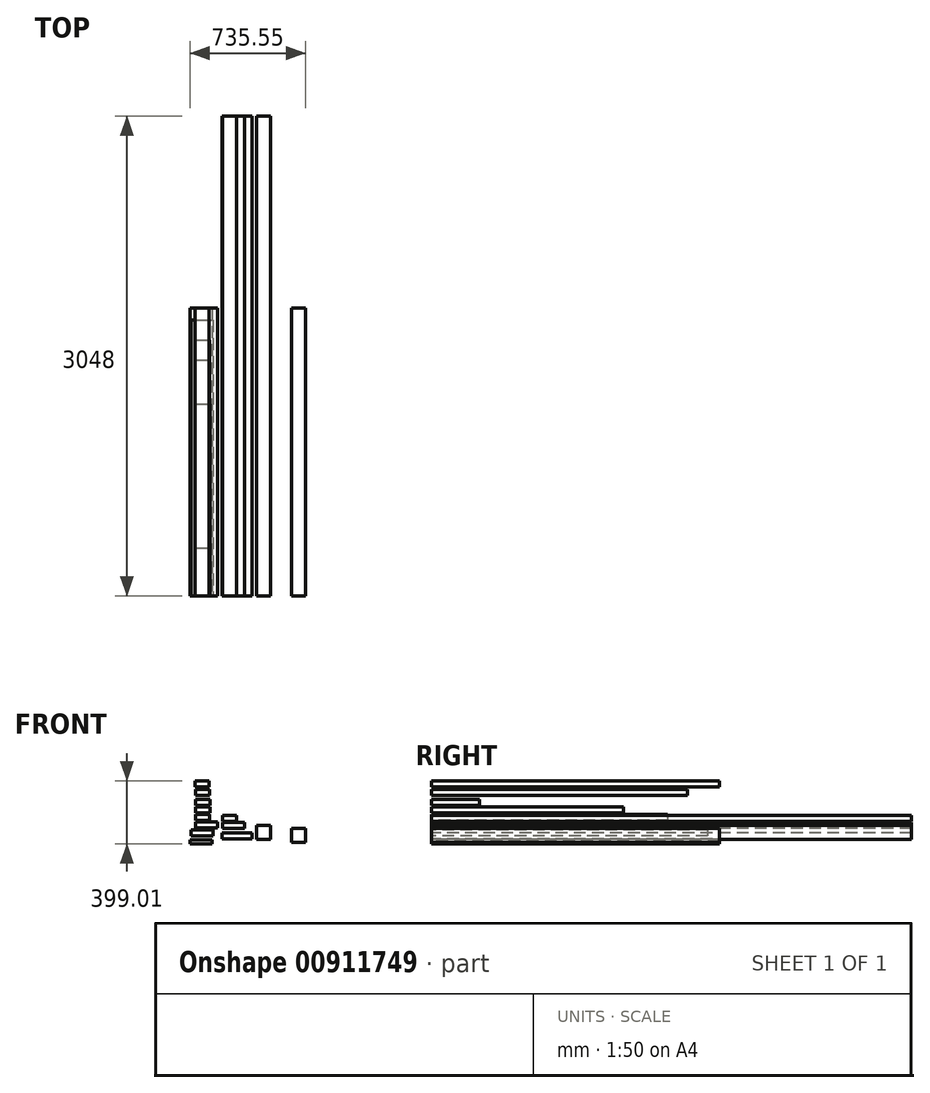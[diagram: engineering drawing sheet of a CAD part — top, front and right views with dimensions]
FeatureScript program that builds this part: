
annotation { "Feature Type Name" : "Feature", "Feature Type Description" : "" }
export const myFeature = defineFeature(function(context is Context, id is Id, definition is map)
    precondition{}
    {
        {
            var Q0;
            Q0=qCreatedBy(makeId("Front.planeOp"),FACE);
            var sketch = newSketch(context, id + "F0", { "sketchPlane" : qUnion([Q0])});
            skLineSegment(sketch, "E0.bottom", {"start": v(-255.68, 9.52) * mm, "end": v(-115.94, 9.52) * mm});
            skLineSegment(sketch, "E0.top", {"start": v(-255.68, -28.56) * mm, "end": v(-115.94, -28.56) * mm});
            skLineSegment(sketch, "E0.left", {"start": v(-255.68, 9.52) * mm, "end": v(-255.68, -28.56) * mm});
            skLineSegment(sketch, "E0.right", {"start": v(-115.94, 9.52) * mm, "end": v(-115.94, -28.56) * mm});
            skLineSegment(sketch, "E1.bottom", {"start": v(-256.83, 16.75) * mm, "end": v(-167.73, 16.75) * mm});
            skLineSegment(sketch, "E1.top", {"start": v(-256.83, 54.83) * mm, "end": v(-167.73, 54.83) * mm});
            skLineSegment(sketch, "E1.left", {"start": v(-256.83, 16.75) * mm, "end": v(-256.83, 54.83) * mm});
            skLineSegment(sketch, "E1.right", {"start": v(-167.73, 16.75) * mm, "end": v(-167.73, 54.83) * mm});
            skLineSegment(sketch, "E2.bottom", {"start": v(-260.63, -58.64) * mm, "end": v(-69.87, -58.64) * mm});
            skLineSegment(sketch, "E2.top", {"start": v(-260.63, -96.71) * mm, "end": v(-69.87, -96.71) * mm});
            skLineSegment(sketch, "E2.left", {"start": v(-260.63, -58.64) * mm, "end": v(-260.63, -96.71) * mm});
            skLineSegment(sketch, "E2.right", {"start": v(-69.87, -58.64) * mm, "end": v(-69.87, -96.71) * mm});
            skLineSegment(sketch, "E3.bottom", {"start": v(-40.93, -10.66) * mm, "end": v(48.17, -10.66) * mm});
            skLineSegment(sketch, "E3.top", {"start": v(-40.93, -99.76) * mm, "end": v(48.17, -99.76) * mm});
            skLineSegment(sketch, "E3.left", {"start": v(-40.93, -10.66) * mm, "end": v(-40.93, -99.76) * mm});
            skLineSegment(sketch, "E3.right", {"start": v(48.17, -10.66) * mm, "end": v(48.17, -99.76) * mm});
            skLineSegment(sketch, "E4.bottom", {"start": v(-448.44, 192.05) * mm, "end": v(-308.7, 192.05) * mm});
            skLineSegment(sketch, "E4.top", {"start": v(-448.44, 153.97) * mm, "end": v(-308.7, 153.97) * mm});
            skLineSegment(sketch, "E4.left", {"start": v(-448.44, 192.05) * mm, "end": v(-448.44, 153.97) * mm});
            skLineSegment(sketch, "E4.right", {"start": v(-308.7, 192.05) * mm, "end": v(-308.7, 153.97) * mm});
            skLineSegment(sketch, "E5.bottom", {"start": v(-449.58, 199.29) * mm, "end": v(-360.48, 199.29) * mm});
            skLineSegment(sketch, "E5.top", {"start": v(-449.58, 237.36) * mm, "end": v(-360.48, 237.36) * mm});
            skLineSegment(sketch, "E5.left", {"start": v(-449.58, 199.29) * mm, "end": v(-449.58, 237.36) * mm});
            skLineSegment(sketch, "E5.right", {"start": v(-360.48, 199.29) * mm, "end": v(-360.48, 237.36) * mm});
            skLineSegment(sketch, "E6.bottom", {"start": v(-453.4, 123.9) * mm, "end": v(-262.63, 123.9) * mm});
            skLineSegment(sketch, "E6.top", {"start": v(-453.4, 85.82) * mm, "end": v(-262.63, 85.82) * mm});
            skLineSegment(sketch, "E6.left", {"start": v(-453.4, 123.9) * mm, "end": v(-453.4, 85.82) * mm});
            skLineSegment(sketch, "E6.right", {"start": v(-262.63, 123.9) * mm, "end": v(-262.63, 85.82) * mm});
            skLineSegment(sketch, "E7.bottom", {"start": v(-233.7, 171.87) * mm, "end": v(-144.6, 171.87) * mm});
            skLineSegment(sketch, "E7.top", {"start": v(-233.7, 82.77) * mm, "end": v(-144.6, 82.77) * mm});
            skLineSegment(sketch, "E7.left", {"start": v(-233.7, 171.87) * mm, "end": v(-233.7, 82.77) * mm});
            skLineSegment(sketch, "E7.right", {"start": v(-144.6, 171.87) * mm, "end": v(-144.6, 82.77) * mm});
            skSolve(sketch);
        }
        {
            var Q0;
            Q0=makeQuery(id+"F0.imprint","IMPRINT",FACE,{"disambiguationData":[TD([[makeQuery(id+"F0.imprint","IMPRINT",EDGE,{"derivedFrom":sQuery(id+"F0.wireOp",EDGE,"E2.bottom")}),-1.0]])]});
            var Q1;
            Q1=makeQuery(id+"F0.imprint","IMPRINT",FACE,{"disambiguationData":[TD([[makeQuery(id+"F0.imprint","IMPRINT",EDGE,{"derivedFrom":sQuery(id+"F0.wireOp",EDGE,"E1.bottom")}),1.0]])]});
            var Q2;
            Q2=makeQuery(id+"F0.imprint","IMPRINT",FACE,{"disambiguationData":[TD([[makeQuery(id+"F0.imprint","IMPRINT",EDGE,{"derivedFrom":sQuery(id+"F0.wireOp",EDGE,"E0.bottom")}),-1.0]])]});
            var Q3;
            Q3=makeQuery(id+"F0.imprint","IMPRINT",FACE,{"disambiguationData":[TD([[makeQuery(id+"F0.imprint","IMPRINT",EDGE,{"derivedFrom":sQuery(id+"F0.wireOp",EDGE,"E3.bottom")}),-1.0]])]});
            var Q4;
            Q4=makeQuery(id+"F0.imprint","IMPRINT",FACE,{"disambiguationData":[TD([[makeQuery(id+"F0.imprint","IMPRINT",EDGE,{"derivedFrom":sQuery(id+"F0.wireOp",EDGE,"E4.bottom")}),-1.0]])]});
            extrude(context, id + "F1", {"entities" : qUnion([Q0, Q1, Q2, Q3, Q4]), "oppositeDirection" : true, "depth" : 3048 * mm, "offsetDistance" : 25.4 * mm});
        }
        {
            var Q0;
            Q0=makeQuery(id+"F1.opExtrude","SWEPT_BODY",BODY,{"disambiguationData":[OSD([sQuery(id+"F0.wireOp",EDGE,"E4.bottom"),sQuery(id+"F0.wireOp",EDGE,"E4.top"),sQuery(id+"F0.wireOp",EDGE,"E4.left"),sQuery(id+"F0.wireOp",EDGE,"E4.right")])]});
            deleteBodies(context, id + "F2", {"entities" : qUnion([Q0])});
        }
        {
            var Q0;
            Q0=makeQuery(id+"F1.opExtrude","CAP_FACE",FACE,{"disambiguationData":[OSD([sQuery(id+"F0.wireOp",EDGE,"E0.bottom"),sQuery(id+"F0.wireOp",EDGE,"E0.top"),sQuery(id+"F0.wireOp",EDGE,"E0.left"),sQuery(id+"F0.wireOp",EDGE,"E0.right")])],"isStart":true});
            var sketch = newSketch(context, id + "F3", { "sketchPlane" : qUnion([Q0])});
            skLineSegment(sketch, "E8.bottom", {"start": v(-427.31, 11.47) * mm, "end": v(-287.75, 11.47) * mm});
            skLineSegment(sketch, "E8.top", {"start": v(-427.31, -26.73) * mm, "end": v(-287.75, -26.73) * mm});
            skLineSegment(sketch, "E8.left", {"start": v(-427.31, 11.47) * mm, "end": v(-427.31, -26.73) * mm});
            skLineSegment(sketch, "E8.right", {"start": v(-287.75, 11.47) * mm, "end": v(-287.75, -26.73) * mm});
            skSolve(sketch);
        }
        {
            var Q0;
            Q0=makeQuery(id+"F3.imprint","IMPRINT",FACE,{"disambiguationData":[TD([[makeQuery(id+"F3.imprint","IMPRINT",EDGE,{"derivedFrom":sQuery(id+"F3.wireOp",EDGE,"E8.bottom")}),-1.0]])]});
            extrude(context, id + "F4", {"entities" : qUnion([Q0]), "oppositeDirection" : true, "depth" : 1828.8 * mm, "offsetDistance" : 25.4 * mm});
        }
        {
            var Q0;
            Q0=makeQuery(id+"F4.opExtrude","CAP_FACE",FACE,{"disambiguationData":[OSD([sQuery(id+"F3.wireOp",EDGE,"E8.bottom"),sQuery(id+"F3.wireOp",EDGE,"E8.top"),sQuery(id+"F3.wireOp",EDGE,"E8.left"),sQuery(id+"F3.wireOp",EDGE,"E8.right")])],"isStart":true});
            var sketch = newSketch(context, id + "F5", { "sketchPlane" : qUnion([Q0])});
            skLineSegment(sketch, "E9.bottom", {"start": v(-456.2, -38.32) * mm, "end": v(-316.88, -38.32) * mm});
            skLineSegment(sketch, "E9.top", {"start": v(-456.2, -76.44) * mm, "end": v(-316.88, -76.44) * mm});
            skLineSegment(sketch, "E9.left", {"start": v(-456.2, -38.32) * mm, "end": v(-456.2, -76.44) * mm});
            skLineSegment(sketch, "E9.right", {"start": v(-316.88, -38.32) * mm, "end": v(-316.88, -76.44) * mm});
            skSolve(sketch);
        }
        {
            var Q0;
            Q0 = qSketchRegion(id + "F5", true);
            extrude(context, id + "F6", {"entities" : qUnion([Q0]), "oppositeDirection" : true, "depth" : 1752.6 * mm, "offsetDistance" : 25.4 * mm});
        }
        {
            var Q0;
            Q0=makeQuery(id+"F4.opExtrude","CAP_FACE",FACE,{"disambiguationData":[OSD([sQuery(id+"F3.wireOp",EDGE,"E8.bottom"),sQuery(id+"F3.wireOp",EDGE,"E8.top"),sQuery(id+"F3.wireOp",EDGE,"E8.left"),sQuery(id+"F3.wireOp",EDGE,"E8.right")])],"isStart":true});
            var sketch = newSketch(context, id + "F7", { "sketchPlane" : qUnion([Q0])});
            skLineSegment(sketch, "E10.bottom", {"start": v(-464.3, -101.85) * mm, "end": v(-323.83, -101.85) * mm});
            skLineSegment(sketch, "E10.top", {"start": v(-464.3, -126.9) * mm, "end": v(-323.83, -126.9) * mm});
            skLineSegment(sketch, "E10.left", {"start": v(-464.3, -101.85) * mm, "end": v(-464.3, -126.9) * mm});
            skLineSegment(sketch, "E10.right", {"start": v(-323.83, -101.85) * mm, "end": v(-323.83, -126.9) * mm});
            skSolve(sketch);
        }
        {
            var Q0;
            Q0 = qSketchRegion(id + "F7", true);
            extrude(context, id + "F8", {"entities" : qUnion([Q0]), "oppositeDirection" : true, "depth" : 1828.8 * mm, "offsetDistance" : 25.4 * mm});
        }
        {
            var Q0;
            Q0=makeQuery(id+"F1.opExtrude","CAP_FACE",FACE,{"disambiguationData":[OSD([sQuery(id+"F0.wireOp",EDGE,"E3.bottom"),sQuery(id+"F0.wireOp",EDGE,"E3.top"),sQuery(id+"F0.wireOp",EDGE,"E3.left"),sQuery(id+"F0.wireOp",EDGE,"E3.right")])],"isStart":true});
            var sketch = newSketch(context, id + "F9", { "sketchPlane" : qUnion([Q0])});
            skLineSegment(sketch, "E11.bottom", {"start": v(182.1, -30.48) * mm, "end": v(271.26, -30.48) * mm});
            skLineSegment(sketch, "E11.top", {"start": v(182.1, -119.56) * mm, "end": v(271.26, -119.56) * mm});
            skLineSegment(sketch, "E11.left", {"start": v(182.1, -30.48) * mm, "end": v(182.1, -119.56) * mm});
            skLineSegment(sketch, "E11.right", {"start": v(271.26, -30.48) * mm, "end": v(271.26, -119.56) * mm});
            skSolve(sketch);
        }
        {
            var Q0;
            Q0 = qSketchRegion(id + "F9", true);
            extrude(context, id + "F10", {"entities" : qUnion([Q0]), "oppositeDirection" : true, "depth" : 1828.8 * mm, "offsetDistance" : 25.4 * mm});
        }
        {
            var Q0;
            Q0=qCreatedBy(makeId("Front.planeOp"),FACE);
            var sketch = newSketch(context, id + "F11", { "sketchPlane" : qUnion([Q0])});
            skLineSegment(sketch, "E12.bottom", {"start": v(-426.6, 155.32) * mm, "end": v(-337.68, 155.32) * mm});
            skLineSegment(sketch, "E12.top", {"start": v(-426.6, 117.07) * mm, "end": v(-337.68, 117.07) * mm});
            skLineSegment(sketch, "E12.left", {"start": v(-426.6, 155.32) * mm, "end": v(-426.6, 117.07) * mm});
            skLineSegment(sketch, "E12.right", {"start": v(-337.68, 155.32) * mm, "end": v(-337.68, 117.07) * mm});
            skSolve(sketch);
        }
        {
            var Q0;
            Q0=makeQuery(id+"F11.imprint","IMPRINT",FACE,{"disambiguationData":[TD([[makeQuery(id+"F11.imprint","IMPRINT",EDGE,{"derivedFrom":sQuery(id+"F11.wireOp",EDGE,"E12.bottom")}),-1.0]])]});
            extrude(context, id + "F12", {"entities" : qUnion([Q0]), "oppositeDirection" : true, "depth" : 304.8 * mm, "offsetDistance" : 25.4 * mm});
        }
        {
            var Q0;
            Q0=qCreatedBy(makeId("Front.planeOp"),FACE);
            var sketch = newSketch(context, id + "F13", { "sketchPlane" : qUnion([Q0])});
            skLineSegment(sketch, "E13.bottom", {"start": v(-426.6, 107.52) * mm, "end": v(-337.68, 107.52) * mm});
            skLineSegment(sketch, "E13.top", {"start": v(-426.6, 69.27) * mm, "end": v(-337.68, 69.27) * mm});
            skLineSegment(sketch, "E13.left", {"start": v(-426.6, 107.52) * mm, "end": v(-426.6, 69.27) * mm});
            skLineSegment(sketch, "E13.right", {"start": v(-337.68, 107.52) * mm, "end": v(-337.68, 69.27) * mm});
            skSolve(sketch);
        }
        {
            var Q0;
            Q0=makeQuery(id+"F13.imprint","IMPRINT",FACE,{"disambiguationData":[TD([[makeQuery(id+"F13.imprint","IMPRINT",EDGE,{"derivedFrom":sQuery(id+"F13.wireOp",EDGE,"E13.bottom")}),-1.0]])]});
            extrude(context, id + "F14", {"entities" : qUnion([Q0]), "oppositeDirection" : true, "depth" : 1219.2 * mm, "offsetDistance" : 25.4 * mm});
        }
        {
            var Q0;
            Q0=qCreatedBy(makeId("Front.planeOp"),FACE);
            var sketch = newSketch(context, id + "F15", { "sketchPlane" : qUnion([Q0])});
            skLineSegment(sketch, "E14.bottom", {"start": v(-428.14, 59.44) * mm, "end": v(-339.23, 59.44) * mm});
            skLineSegment(sketch, "E14.top", {"start": v(-428.14, 21.19) * mm, "end": v(-339.23, 21.19) * mm});
            skLineSegment(sketch, "E14.left", {"start": v(-428.14, 59.44) * mm, "end": v(-428.14, 21.19) * mm});
            skLineSegment(sketch, "E14.right", {"start": v(-339.23, 59.44) * mm, "end": v(-339.23, 21.19) * mm});
            skSolve(sketch);
        }
        {
            var Q0;
            Q0=makeQuery(id+"F15.imprint","IMPRINT",FACE,{"disambiguationData":[TD([[makeQuery(id+"F15.imprint","IMPRINT",EDGE,{"derivedFrom":sQuery(id+"F15.wireOp",EDGE,"E14.bottom")}),-1.0]])]});
            extrude(context, id + "F16", {"entities" : qUnion([Q0]), "oppositeDirection" : true, "depth" : 1498.6 * mm, "offsetDistance" : 25.4 * mm});
        }
        {
            var Q0;
            Q0=qCreatedBy(makeId("Front.planeOp"),FACE);
            var sketch = newSketch(context, id + "F17", { "sketchPlane" : qUnion([Q0])});
            skLineSegment(sketch, "E15.bottom", {"start": v(-428.14, 218.15) * mm, "end": v(-339.23, 218.15) * mm});
            skLineSegment(sketch, "E15.top", {"start": v(-428.14, 179.9) * mm, "end": v(-339.23, 179.9) * mm});
            skLineSegment(sketch, "E15.left", {"start": v(-428.14, 218.15) * mm, "end": v(-428.14, 179.9) * mm});
            skLineSegment(sketch, "E15.right", {"start": v(-339.23, 218.15) * mm, "end": v(-339.23, 179.9) * mm});
            skSolve(sketch);
        }
        {
            var Q0;
            Q0=makeQuery(id+"F17.imprint","IMPRINT",FACE,{"disambiguationData":[TD([[makeQuery(id+"F17.imprint","IMPRINT",EDGE,{"derivedFrom":sQuery(id+"F17.wireOp",EDGE,"E15.bottom")}),-1.0]])]});
            extrude(context, id + "F18", {"entities" : qUnion([Q0]), "oppositeDirection" : true, "depth" : 1625.6 * mm, "offsetDistance" : 25.4 * mm});
        }
        {
            var Q0;
            Q0=qCreatedBy(makeId("Front.planeOp"),FACE);
            var sketch = newSketch(context, id + "F19", { "sketchPlane" : qUnion([Q0])});
            skLineSegment(sketch, "E16.bottom", {"start": v(-430.43, 272.1) * mm, "end": v(-341.32, 272.1) * mm});
            skLineSegment(sketch, "E16.top", {"start": v(-430.43, 233.85) * mm, "end": v(-341.32, 233.85) * mm});
            skLineSegment(sketch, "E16.left", {"start": v(-430.43, 272.1) * mm, "end": v(-430.43, 233.85) * mm});
            skLineSegment(sketch, "E16.right", {"start": v(-341.32, 272.1) * mm, "end": v(-341.32, 233.85) * mm});
            skSolve(sketch);
        }
        {
            var Q0;
            Q0=makeQuery(id+"F19.imprint","IMPRINT",FACE,{"disambiguationData":[TD([[makeQuery(id+"F19.imprint","IMPRINT",EDGE,{"derivedFrom":sQuery(id+"F19.wireOp",EDGE,"E16.bottom")}),-1.0]])]});
            extrude(context, id + "F20", {"entities" : qUnion([Q0]), "oppositeDirection" : true, "depth" : 1828.8 * mm, "offsetDistance" : 25.4 * mm});
        }
    });
